# Revit family: Keilhauer_Juxta_Benches_Stools_Star_Low_Back_Stool-
name_source: partatom
category: Furniture
revit_build: Autodesk Revit 2016 (Build: 20150220_1215(x64)
units: mm (PartAtom-declared; Revit-internal decimal feet)

## family parameters
Always vertical = Yes
Cut with Voids When Loaded = No
OmniClass Number = 23.40.70.14.64.11
OmniClass Title = Office Furniture
Room Calculation Point = No
Shared = No
Work Plane-Based = No

## types (4) — shared parameters
Assembly Code = E2020200
Catalog = JUXTA
Keynote = 12500
Manufacturer = Keilhauer, Corp.
Product Documentation Link = https://keilhauer.com
Revit Model Built By = https://servex-us.com
URL = http://www.keilhauer.com

## per-type parameters (varying)
| type | Description | Five Star | Four Leg | Seat Height |
| 46612 | Low Back Armless, 4 Leg Counter Stool | No | Yes | 21 5/8" |
| 46613 | Low Back Armless, 4 Leg Bar Stool | No | Yes | 25 5/8" |
| 46652 | Low Back Armless, 5 Star Counter Stool With Ring, Casters | Yes | No | 21 5/8" |
| 46653 | Low Back Armless, 5 Star Bar Stool With Ring, Casters | Yes | No | 25 5/8" |

note: column(s) folded — value = type name in every type: Model

## geometry (parser evidence)
native form markers: Sweep x5
no freeform markers — native parametric forms only
